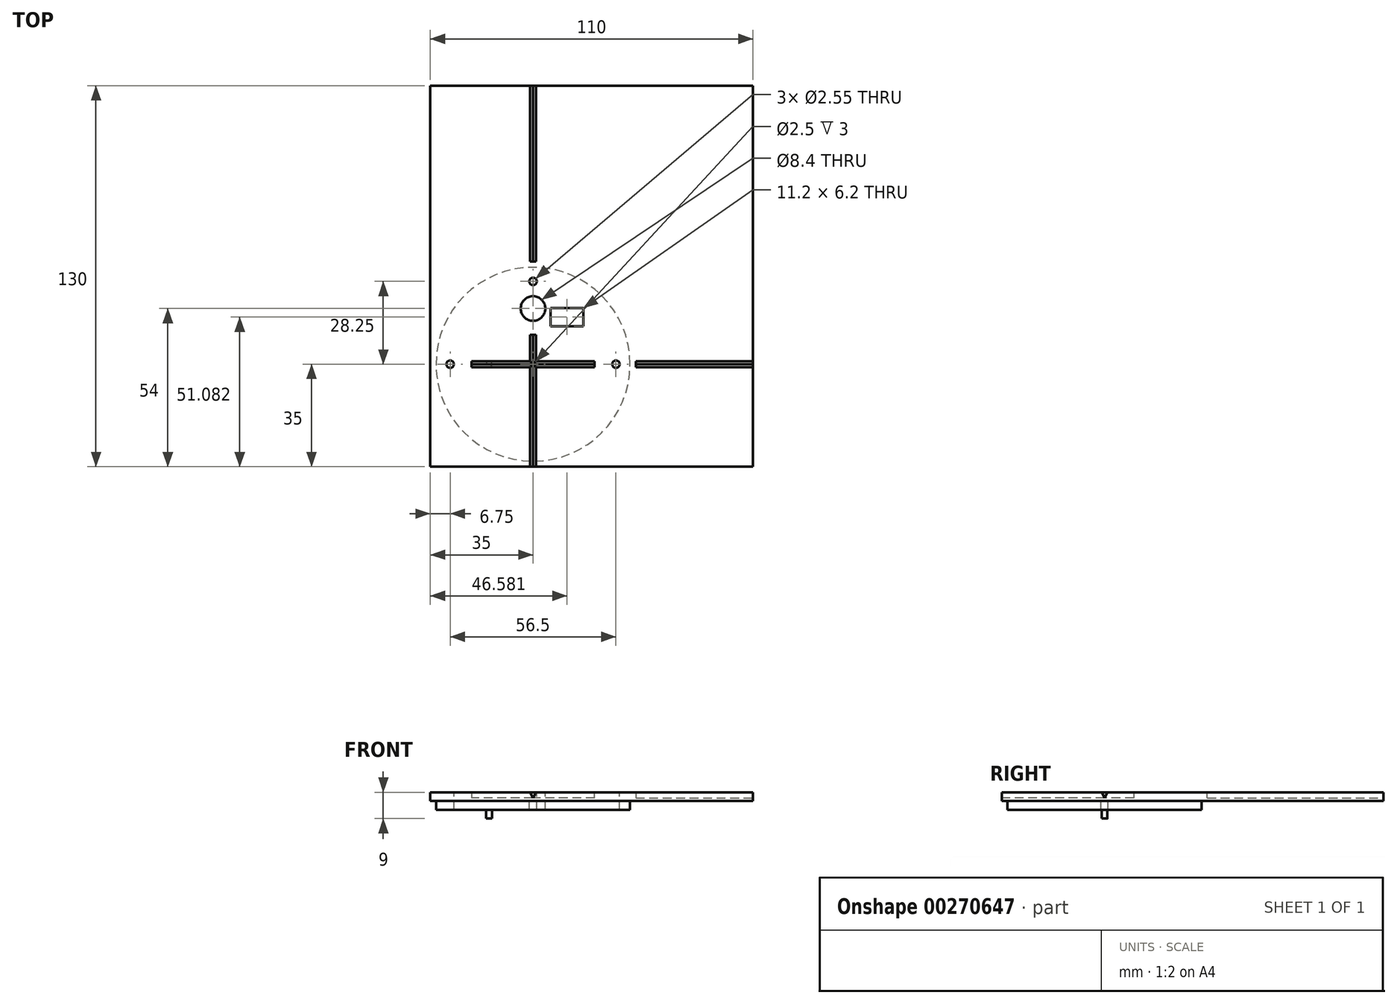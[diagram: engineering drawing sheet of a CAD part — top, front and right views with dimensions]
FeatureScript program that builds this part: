
annotation { "Feature Type Name" : "Feature", "Feature Type Description" : "" }
export const myFeature = defineFeature(function(context is Context, id is Id, definition is map)
    precondition{}
    {
        {
            var Q0;
            Q0=qCreatedBy(makeId("Top.planeOp"),FACE);
            var sketch = newSketch(context, id + "F0", { "sketchPlane" : qUnion([Q0])});
            skPoint(sketch, "E0.4", {"position": v(0, 0) * mm});
            skCircle(sketch, "E1", {"center": v(0, 0) * mm, "radius": 33.07 * mm});
            skPoint(sketch, "E2", {"position": v(-28.25, 0) * mm});
            skPoint(sketch, "E3", {"position": v(-15, 0) * mm});
            skPoint(sketch, "E4", {"position": v(0, 19) * mm});
            skPoint(sketch, "E5", {"position": v(0, 28.25) * mm});
            skCircle(sketch, "E6", {"center": v(0, 0) * mm, "radius": 1.25 * mm});
            skCircle(sketch, "E7", {"center": v(0, 19) * mm, "radius": 4.2 * mm});
            skLineSegment(sketch, "E8.bottom", {"start": v(5.98, 12.98) * mm, "end": v(17.18, 12.98) * mm});
            skLineSegment(sketch, "E8.top", {"start": v(5.98, 19.18) * mm, "end": v(17.18, 19.18) * mm});
            skLineSegment(sketch, "E8.left", {"start": v(5.98, 12.98) * mm, "end": v(5.98, 19.18) * mm});
            skLineSegment(sketch, "E8.right", {"start": v(17.18, 12.98) * mm, "end": v(17.18, 19.18) * mm});
            skPoint(sketch, "E9", {"position": v(17.18, 19.18) * mm});
            skPoint(sketch, "E10", {"position": v(5.98, 12.98) * mm});
            skLineSegment(sketch, "E11", {"start": v(21.45, 16.08) * mm, "end": v(-17.9, 16.08) * mm, "construction": true});
            skLineSegment(sketch, "E12", {"start": v(11.58, 19.58) * mm, "end": v(11.58, -2.2) * mm, "construction": true});
            skCircle(sketch, "E13", {"center": v(-15, 0) * mm, "radius": 1 * mm});
            skCircle(sketch, "E14", {"center": v(-28.25, 0) * mm, "radius": 1.02 * mm});
            skCircle(sketch, "E15", {"center": v(-28.25, 0) * mm, "radius": 1.28 * mm});
            skCircle(sketch, "E16.MirrorC", {"center": v(28.25, 0) * mm, "radius": 1.02 * mm});
            skCircle(sketch, "E17.MirrorC", {"center": v(28.25, 0) * mm, "radius": 1.28 * mm});
            skLineSegment(sketch, "E18.bottom", {"start": v(60, 80) * mm, "end": v(-20, 80) * mm});
            skLineSegment(sketch, "E18.top", {"start": v(60, -20) * mm, "end": v(-20, -20) * mm});
            skLineSegment(sketch, "E18.left", {"start": v(60, 80) * mm, "end": v(60, -20) * mm});
            skLineSegment(sketch, "E18.right", {"start": v(-20, 80) * mm, "end": v(-20, -20) * mm});
            skLineSegment(sketch, "E19.bottom", {"start": v(75, 95) * mm, "end": v(-35, 95) * mm});
            skLineSegment(sketch, "E19.top", {"start": v(75, -35) * mm, "end": v(-35, -35) * mm});
            skLineSegment(sketch, "E19.left", {"start": v(75, 95) * mm, "end": v(75, -35) * mm});
            skLineSegment(sketch, "E19.right", {"start": v(-35, 95) * mm, "end": v(-35, -35) * mm});
            skCircle(sketch, "E20", {"center": v(0, 28.25) * mm, "radius": 1.28 * mm});
            skCircle(sketch, "E21", {"center": v(0, 28.25) * mm, "radius": 1.02 * mm});
            skSolve(sketch);
        }
        {
            var Q0;
            Q0=makeQuery(id+"F0.imprint","IMPRINT",FACE,{"disambiguationData":[TD([[makeQuery(id+"F0.imprint","IMPRINT",EDGE,{"derivedFrom":sQuery(id+"F0.wireOp",EDGE,"E6")}),-1.0]])]});
            var Q1;
            Q1=makeQuery(id+"F0.imprint","IMPRINT",FACE,{"disambiguationData":[TD([[makeQuery(id+"F0.imprint","IMPRINT",EDGE,{"derivedFrom":sQuery(id+"F0.wireOp",EDGE,"E15")}),-1.0]])]});
            extrude(context, id + "F1", {"entities" : qUnion([Q0, Q1]), "oppositeDirection" : true, "depth" : 3 * mm});
        }
        {
            var Q0;
            {var subQ4=sQuery(id+"F0.wireOp",EDGE,"E18.bottom");Q0=makeQuery(id+"F0.imprint","IMPRINT",FACE,{"disambiguationData":[TD([[makeQuery(id+"F0.imprint","IMPRINT",EDGE,{"derivedFrom":subQ4}),-1.0]])]});}
            var Q1;
            Q1=makeQuery(id+"F0.imprint","IMPRINT",FACE,{"disambiguationData":[TD([[makeQuery(id+"F0.imprint","IMPRINT",EDGE,{"derivedFrom":sQuery(id+"F0.wireOp",EDGE,"E6")}),-1.0]])]});
            var Q2;
            Q2=makeQuery(id+"F0.imprint","IMPRINT",FACE,{"disambiguationData":[TD([[makeQuery(id+"F0.imprint","IMPRINT",EDGE,{"derivedFrom":sQuery(id+"F0.wireOp",EDGE,"E15")}),-1.0]])]});
            var Q3;
            {var subQ4=sQuery(id+"F0.wireOp",EDGE,"E18.bottom");Q3=makeQuery(id+"F0.imprint","IMPRINT",FACE,{"disambiguationData":[TD([[makeQuery(id+"F0.imprint","IMPRINT",EDGE,{"derivedFrom":subQ4}),1.0]])]});}
            var Q4;
            Q4=makeQuery(id+"F0.imprint","IMPRINT",FACE,{"disambiguationData":[TD([[makeQuery(id+"F0.imprint","IMPRINT",EDGE,{"derivedFrom":sQuery(id+"F0.wireOp",EDGE,"E13")}),1.0]])]});
            var Q5;
            Q5=makeQuery(id+"F0.imprint","IMPRINT",FACE,{"disambiguationData":[TD([[makeQuery(id+"F0.imprint","IMPRINT",EDGE,{"derivedFrom":sQuery(id+"F0.wireOp",EDGE,"E6")}),1.0]])]});
            extrude(context, id + "F2", {"entities" : qUnion([Q0, Q1, Q2, Q3, Q4, Q5]), "operationType" : NewBodyOperationType.ADD, "depth" : 3 * mm});
        }
        {
            var Q0;
            Q0=makeQuery(id+"F0.imprint","IMPRINT",FACE,{"disambiguationData":[TD([[makeQuery(id+"F0.imprint","IMPRINT",EDGE,{"derivedFrom":sQuery(id+"F0.wireOp",EDGE,"E13")}),1.0]])]});
            extrude(context, id + "F3", {"entities" : qUnion([Q0]), "operationType" : NewBodyOperationType.ADD, "oppositeDirection" : true, "depth" : 6 * mm});
        }
        {
            var Q0;
            Q0=makeQuery(id+"F2.opExtrude","SWEPT_FACE",FACE,{"disambiguationData":[OSD([sQuery(id+"F0.wireOp",EDGE,"E19.top")])]});
            var sketch = newSketch(context, id + "F4", { "sketchPlane" : qUnion([Q0])});
            skLineSegment(sketch, "E22", {"start": v(-1, 3) * mm, "end": v(0, 1) * mm});
            skLineSegment(sketch, "E23", {"start": v(0, 1) * mm, "end": v(1, 3) * mm});
            skLineSegment(sketch, "E24", {"start": v(1, 3) * mm, "end": v(-1, 3) * mm});
            skSolve(sketch);
        }
        {
            var Q0;
            Q0 = qSketchRegion(id + "F4", true);
            extrude(context, id + "F5", {"entities" : qUnion([Q0]), "operationType" : NewBodyOperationType.REMOVE, "oppositeDirection" : true, "depth" : 45 * mm});
        }
        {
            var Q0;
            Q0=makeQuery(id+"F2.opExtrude","SWEPT_FACE",FACE,{"disambiguationData":[OSD([sQuery(id+"F0.wireOp",EDGE,"E19.bottom")])]});
            var sketch = newSketch(context, id + "F6", { "sketchPlane" : qUnion([Q0])});
            skLineSegment(sketch, "E25.0", {"start": v(0, 1) * mm, "end": v(-1, 3) * mm});
            skLineSegment(sketch, "E25.1", {"start": v(1, 3) * mm, "end": v(0, 1) * mm});
            skLineSegment(sketch, "E26", {"start": v(-1, 3) * mm, "end": v(0, 1) * mm});
            skLineSegment(sketch, "E27", {"start": v(1, 3) * mm, "end": v(-1, 3) * mm});
            skSolve(sketch);
        }
        {
            var Q0;
            Q0 = qSketchRegion(id + "F6", true);
            extrude(context, id + "F7", {"entities" : qUnion([Q0]), "operationType" : NewBodyOperationType.REMOVE, "oppositeDirection" : true, "depth" : 60 * mm});
        }
        {
            var Q0;
            Q0=makeQuery(id+"F2.opExtrude","SWEPT_FACE",FACE,{"disambiguationData":[OSD([sQuery(id+"F0.wireOp",EDGE,"E19.left")])]});
            var sketch = newSketch(context, id + "F8", { "sketchPlane" : qUnion([Q0])});
            skLineSegment(sketch, "E28", {"start": v(-1, 3) * mm, "end": v(0, 1) * mm});
            skLineSegment(sketch, "E29", {"start": v(0, 1) * mm, "end": v(1, 3) * mm});
            skLineSegment(sketch, "E30", {"start": v(1, 3) * mm, "end": v(-1, 3) * mm});
            skSolve(sketch);
        }
        {
            var Q0;
            Q0=makeQuery(id+"F8.imprint","IMPRINT",FACE,{"disambiguationData":[TD([[makeQuery(id+"F8.imprint","IMPRINT",EDGE,{"derivedFrom":sQuery(id+"F8.wireOp",EDGE,"E28")}),1.0]])]});
            extrude(context, id + "F9", {"entities" : qUnion([Q0]), "operationType" : NewBodyOperationType.REMOVE, "oppositeDirection" : true, "depth" : 40 * mm});
        }
        {
            var Q0;
            Q0=qCreatedBy(makeId("Right.planeOp"),FACE);
            var sketch = newSketch(context, id + "F10", { "sketchPlane" : qUnion([Q0])});
            skLineSegment(sketch, "E31.0", {"start": v(0, 1) * mm, "end": v(1, 3) * mm});
            skLineSegment(sketch, "E32.0", {"start": v(1, 3) * mm, "end": v(-1, 3) * mm});
            skLineSegment(sketch, "E33.0", {"start": v(-1, 3) * mm, "end": v(0, 1) * mm});
            skSolve(sketch);
        }
        {
            var Q0;
            Q0=makeQuery(id+"F10.imprint","IMPRINT",FACE,{"disambiguationData":[TD([[makeQuery(id+"F10.imprint","IMPRINT",EDGE,{"derivedFrom":sQuery(id+"F10.wireOp",EDGE,"E31.0")}),1.0]])]});
            extrude(context, id + "F11", {"entities" : qUnion([Q0]), "operationType" : NewBodyOperationType.REMOVE, "endBound" : BoundingType.SYMMETRIC, "depth" : 42 * mm});
        }
    });
